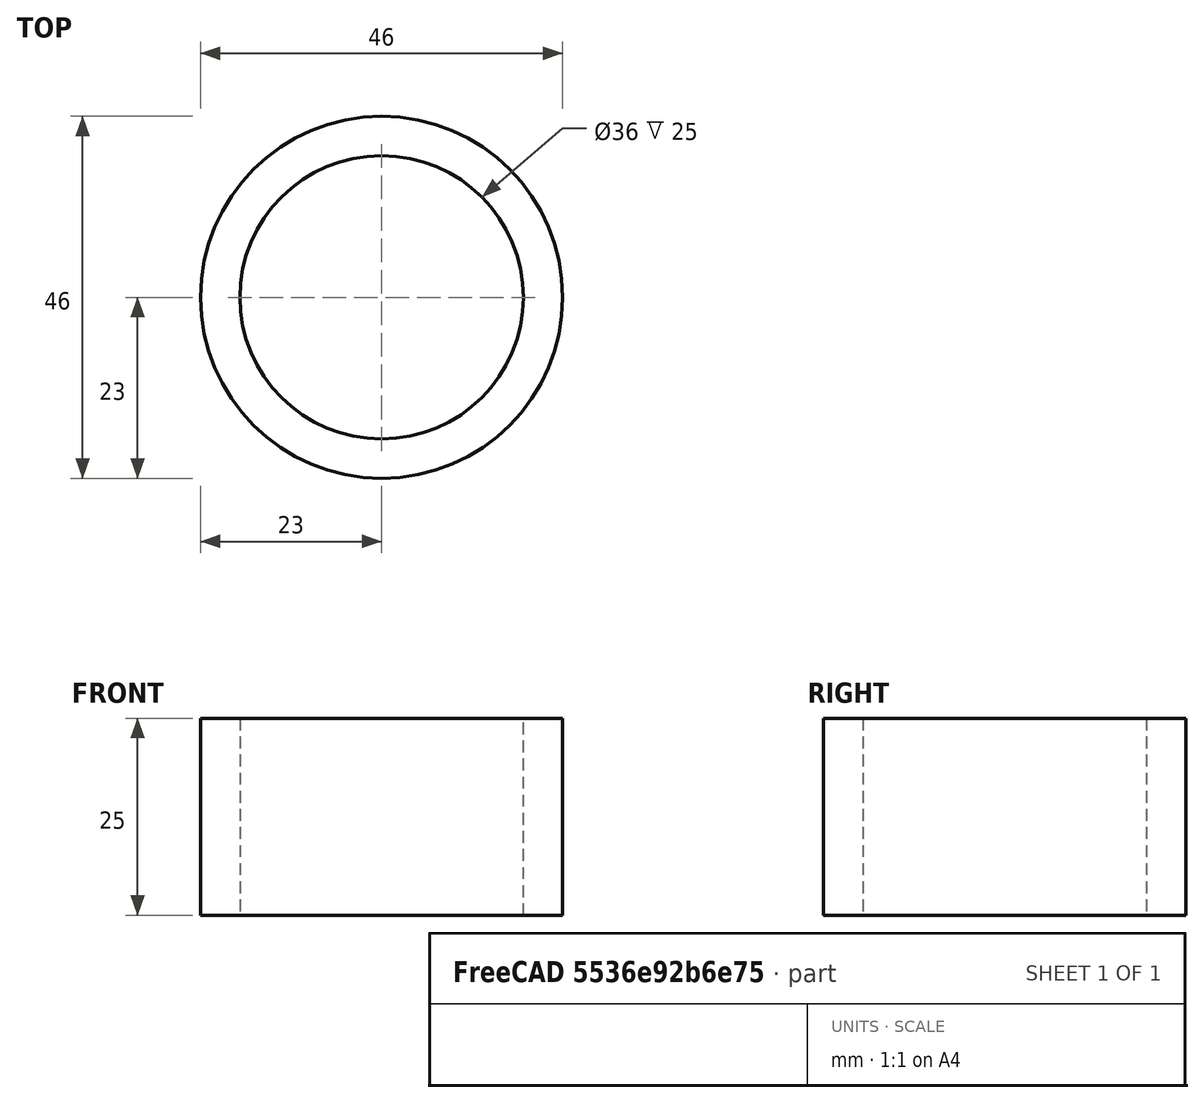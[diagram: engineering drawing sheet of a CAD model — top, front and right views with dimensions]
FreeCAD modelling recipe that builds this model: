
FCSTD DOCUMENT  (FreeCAD 0.21R33668 +26 (Git))
Label: neumático
License: All rights reserved
LicenseURL: https://en.wikipedia.org/wiki/All_rights_reserved
objects: Sketcher::SketchObject×1, PartDesign::Pad×1, PartDesign::Body×1
note: 4 computed .brp shape members not serialized (recipe doc carries the construction recipe); baked Part::Feature solids carry a one-line shape summary decoded from their .brp

FEATURE [Sketcher::SketchObject] Sketch
  FullyConstrained = true
  MapMode = 5
  Support = -> [XY_Plane]
  sketch-geometry (2):
    g0: Circle CenterX=0 CenterY=0 CenterZ=0 NormalX=0 NormalY=0 NormalZ=1 AngleXU=0 Radius=18
    g1: Circle CenterX=0 CenterY=0 CenterZ=0 NormalX=0 NormalY=0 NormalZ=1 AngleXU=0 Radius=23
  constraints (4):
    c: Coincident(g0,g-1)
    c: Diameter(g0) = 36
    c: Coincident(g1,g0)
    c: Diameter(g1) = 46
FEATURE [PartDesign::Pad] Pad  label="base"
  Direction = (0,0,1)
  Length = 25
  Length2 = 10
  Profile = -> Sketch
  ReferenceAxis = -> Sketch [N_Axis]
  Type = 0
FEATURE [PartDesign::Body] Body  label="Cuerpo"
  Group = -> [Sketch,Pad]
  Origin = -> Origin
  Tip = -> Pad
